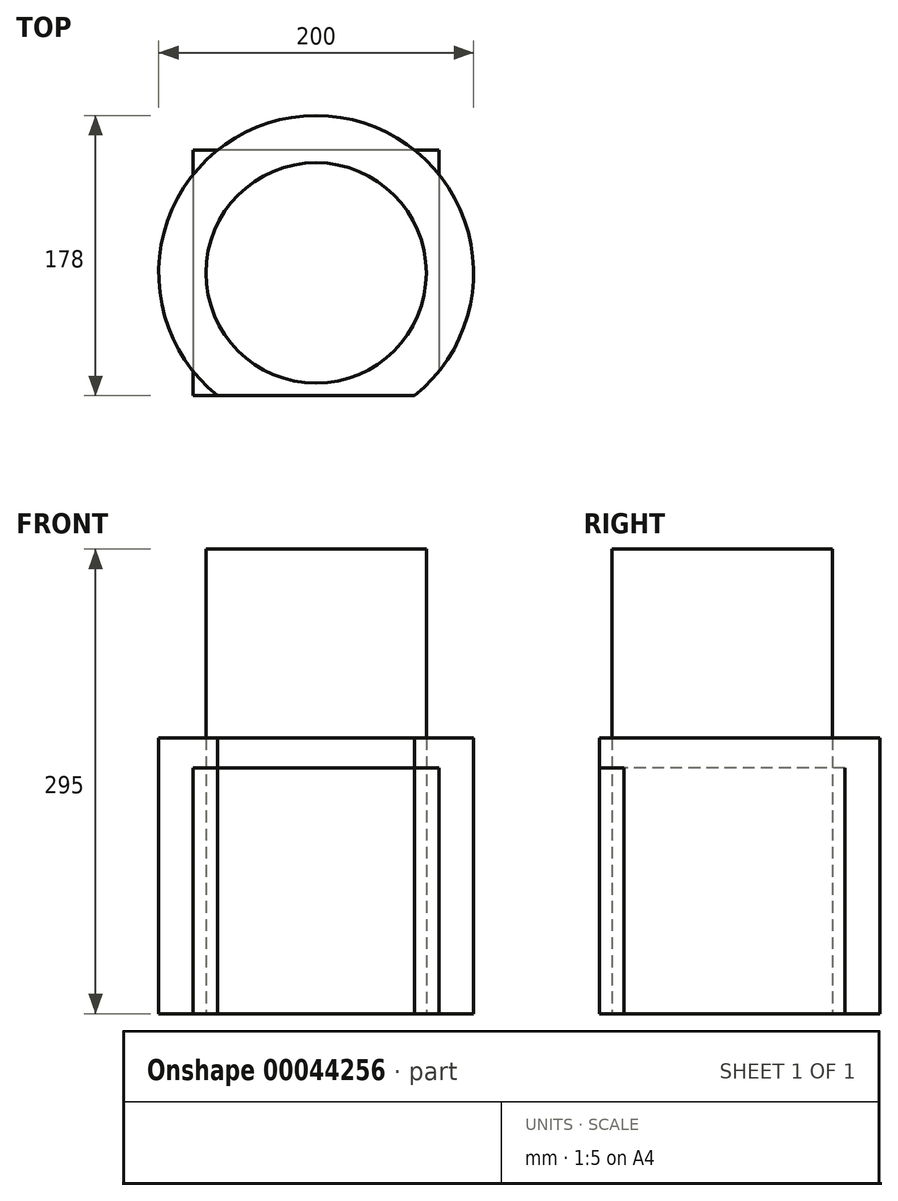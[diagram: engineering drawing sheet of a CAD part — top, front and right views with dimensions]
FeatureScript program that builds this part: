
annotation { "Feature Type Name" : "Feature", "Feature Type Description" : "" }
export const myFeature = defineFeature(function(context is Context, id is Id, definition is map)
    precondition{}
    {
        {
            var Q0;
            Q0=qCreatedBy(makeId("Top.planeOp"),FACE);
            var sketch = newSketch(context, id + "F0", { "sketchPlane" : qUnion([Q0])});
            skCircle(sketch, "E0", {"center": v(0, 0) * mm, "radius": 100 * mm});
            skLineSegment(sketch, "E1.bottom", {"start": v(78, 78) * mm, "end": v(-78, 78) * mm});
            skLineSegment(sketch, "E1.top", {"start": v(78, -78) * mm, "end": v(-78, -78) * mm});
            skLineSegment(sketch, "E1.left", {"start": v(78, 78) * mm, "end": v(78, -78) * mm});
            skLineSegment(sketch, "E1.right", {"start": v(-78, 78) * mm, "end": v(-78, -78) * mm});
            skCircle(sketch, "E2", {"center": v(0, 0) * mm, "radius": 70 * mm});
            skSolve(sketch);
        }
        {
            var Q0;
            {var subQ0=sQuery(id+"F0.wireOp",EDGE,"E1.bottom");var subQ1=sQuery(id+"F0.wireOp",EDGE,"E0");var subQ2=makeQuery(id+"F0.imprint","INTERSECT",VERTEX,{"disambiguationData":[OD(1.0)],"derivedFrom":[subQ1,subQ0]});Q0=makeQuery(id+"F0.imprint","IMPRINT",FACE,{"disambiguationData":[TD([[makeQuery(id+"F0.imprint","IMPRINT",EDGE,{"disambiguationData":[TD([[subQ2,-1.0]])],"derivedFrom":subQ1}),-1.0]])]});}
            var Q1;
            {var subQ1=sQuery(id+"F0.wireOp",EDGE,"E0");var subQ9=sQuery(id+"F0.wireOp",EDGE,"E1.bottom");var subQ12=makeQuery(id+"F0.imprint","INTERSECT",VERTEX,{"disambiguationData":[OD(0.0)],"derivedFrom":[subQ1,subQ9]});Q1=makeQuery(id+"F0.imprint","IMPRINT",FACE,{"disambiguationData":[TD([[makeQuery(id+"F0.imprint","IMPRINT",EDGE,{"disambiguationData":[TD([[subQ12,1.0]])],"derivedFrom":subQ1}),1.0]])]});}
            var Q2;
            {var subQ0=sQuery(id+"F0.wireOp",EDGE,"E1.bottom");var subQ1=sQuery(id+"F0.wireOp",EDGE,"E0");var subQ2=makeQuery(id+"F0.imprint","INTERSECT",VERTEX,{"disambiguationData":[OD(0.0)],"derivedFrom":[subQ1,subQ0]});Q2=makeQuery(id+"F0.imprint","IMPRINT",FACE,{"disambiguationData":[TD([[makeQuery(id+"F0.imprint","IMPRINT",EDGE,{"disambiguationData":[TD([[subQ2,1.0]])],"derivedFrom":subQ1}),-1.0]])]});}
            var Q3;
            {var subQ0=sQuery(id+"F0.wireOp",EDGE,"E1.right");var subQ1=sQuery(id+"F0.wireOp",EDGE,"E0");var subQ2=makeQuery(id+"F0.imprint","INTERSECT",VERTEX,{"disambiguationData":[OD(1.0)],"derivedFrom":[subQ1,subQ0]});Q3=makeQuery(id+"F0.imprint","IMPRINT",FACE,{"disambiguationData":[TD([[makeQuery(id+"F0.imprint","IMPRINT",EDGE,{"disambiguationData":[TD([[subQ2,-1.0]])],"derivedFrom":subQ1}),-1.0]])]});}
            var Q4;
            {var subQ0=sQuery(id+"F0.wireOp",EDGE,"E1.top");var subQ1=sQuery(id+"F0.wireOp",EDGE,"E0");var subQ2=makeQuery(id+"F0.imprint","INTERSECT",VERTEX,{"disambiguationData":[OD(1.0)],"derivedFrom":[subQ1,subQ0]});Q4=makeQuery(id+"F0.imprint","IMPRINT",FACE,{"disambiguationData":[TD([[makeQuery(id+"F0.imprint","IMPRINT",EDGE,{"disambiguationData":[TD([[subQ2,-1.0]])],"derivedFrom":subQ1}),-1.0]])]});}
            var Q5;
            Q5=makeQuery(id+"F0.imprint","IMPRINT",FACE,{"disambiguationData":[TD([[makeQuery(id+"F0.imprint","IMPRINT",EDGE,{"derivedFrom":sQuery(id+"F0.wireOp",EDGE,"E2")}),1.0]])]});
            extrude(context, id + "F1", {"entities" : qUnion([Q0, Q1, Q2, Q3, Q4, Q5]), "depth" : 156 * mm, "offsetDistance" : 25 * mm});
        }
        {
            var Q0;
            {var subQ0=sQuery(id+"F0.wireOp",EDGE,"E1.right");var subQ1=sQuery(id+"F0.wireOp",EDGE,"E0");var subQ2=makeQuery(id+"F0.imprint","INTERSECT",VERTEX,{"disambiguationData":[OD(0.0)],"derivedFrom":[subQ1,subQ0]});Q0=makeQuery(id+"F0.imprint","IMPRINT",FACE,{"disambiguationData":[TD([[makeQuery(id+"F0.imprint","IMPRINT",EDGE,{"disambiguationData":[TD([[subQ2,-1.0]])],"derivedFrom":subQ1}),1.0]])]});}
            var Q1;
            {var subQ1=sQuery(id+"F0.wireOp",EDGE,"E0");var subQ9=sQuery(id+"F0.wireOp",EDGE,"E1.bottom");var subQ12=makeQuery(id+"F0.imprint","INTERSECT",VERTEX,{"disambiguationData":[OD(0.0)],"derivedFrom":[subQ1,subQ9]});Q1=makeQuery(id+"F0.imprint","IMPRINT",FACE,{"disambiguationData":[TD([[makeQuery(id+"F0.imprint","IMPRINT",EDGE,{"disambiguationData":[TD([[subQ12,1.0]])],"derivedFrom":subQ1}),1.0]])]});}
            var Q2;
            {var subQ0=sQuery(id+"F0.wireOp",EDGE,"E1.top");var subQ1=sQuery(id+"F0.wireOp",EDGE,"E0");var subQ2=makeQuery(id+"F0.imprint","INTERSECT",VERTEX,{"disambiguationData":[OD(0.0)],"derivedFrom":[subQ1,subQ0]});Q2=makeQuery(id+"F0.imprint","IMPRINT",FACE,{"disambiguationData":[TD([[makeQuery(id+"F0.imprint","IMPRINT",EDGE,{"disambiguationData":[TD([[subQ2,-1.0]])],"derivedFrom":subQ1}),1.0]])]});}
            var Q3;
            {var subQ0=sQuery(id+"F0.wireOp",EDGE,"E1.left");var subQ1=sQuery(id+"F0.wireOp",EDGE,"E0");var subQ2=makeQuery(id+"F0.imprint","INTERSECT",VERTEX,{"disambiguationData":[OD(0.0)],"derivedFrom":[subQ1,subQ0]});Q3=makeQuery(id+"F0.imprint","IMPRINT",FACE,{"disambiguationData":[TD([[makeQuery(id+"F0.imprint","IMPRINT",EDGE,{"disambiguationData":[TD([[subQ2,1.0]])],"derivedFrom":subQ1}),1.0]])]});}
            var Q4;
            {var subQ0=sQuery(id+"F0.wireOp",EDGE,"E1.bottom");var subQ1=sQuery(id+"F0.wireOp",EDGE,"E0");var subQ2=makeQuery(id+"F0.imprint","INTERSECT",VERTEX,{"disambiguationData":[OD(0.0)],"derivedFrom":[subQ1,subQ0]});Q4=makeQuery(id+"F0.imprint","IMPRINT",FACE,{"disambiguationData":[TD([[makeQuery(id+"F0.imprint","IMPRINT",EDGE,{"disambiguationData":[TD([[subQ2,-1.0]])],"derivedFrom":subQ1}),1.0]])]});}
            var Q5;
            Q5=makeQuery(id+"F0.imprint","IMPRINT",FACE,{"disambiguationData":[TD([[makeQuery(id+"F0.imprint","IMPRINT",EDGE,{"derivedFrom":sQuery(id+"F0.wireOp",EDGE,"E2")}),1.0]])]});
            extrude(context, id + "F2", {"entities" : qUnion([Q0, Q1, Q2, Q3, Q4, Q5]), "depth" : 175 * mm, "offsetDistance" : 25 * mm});
        }
        {
            var Q0;
            Q0=makeQuery(id+"F0.imprint","IMPRINT",FACE,{"disambiguationData":[TD([[makeQuery(id+"F0.imprint","IMPRINT",EDGE,{"derivedFrom":sQuery(id+"F0.wireOp",EDGE,"E2")}),1.0]])]});
            extrude(context, id + "F3", {"entities" : qUnion([Q0]), "depth" : 295 * mm, "offsetDistance" : 25 * mm});
        }
    });
